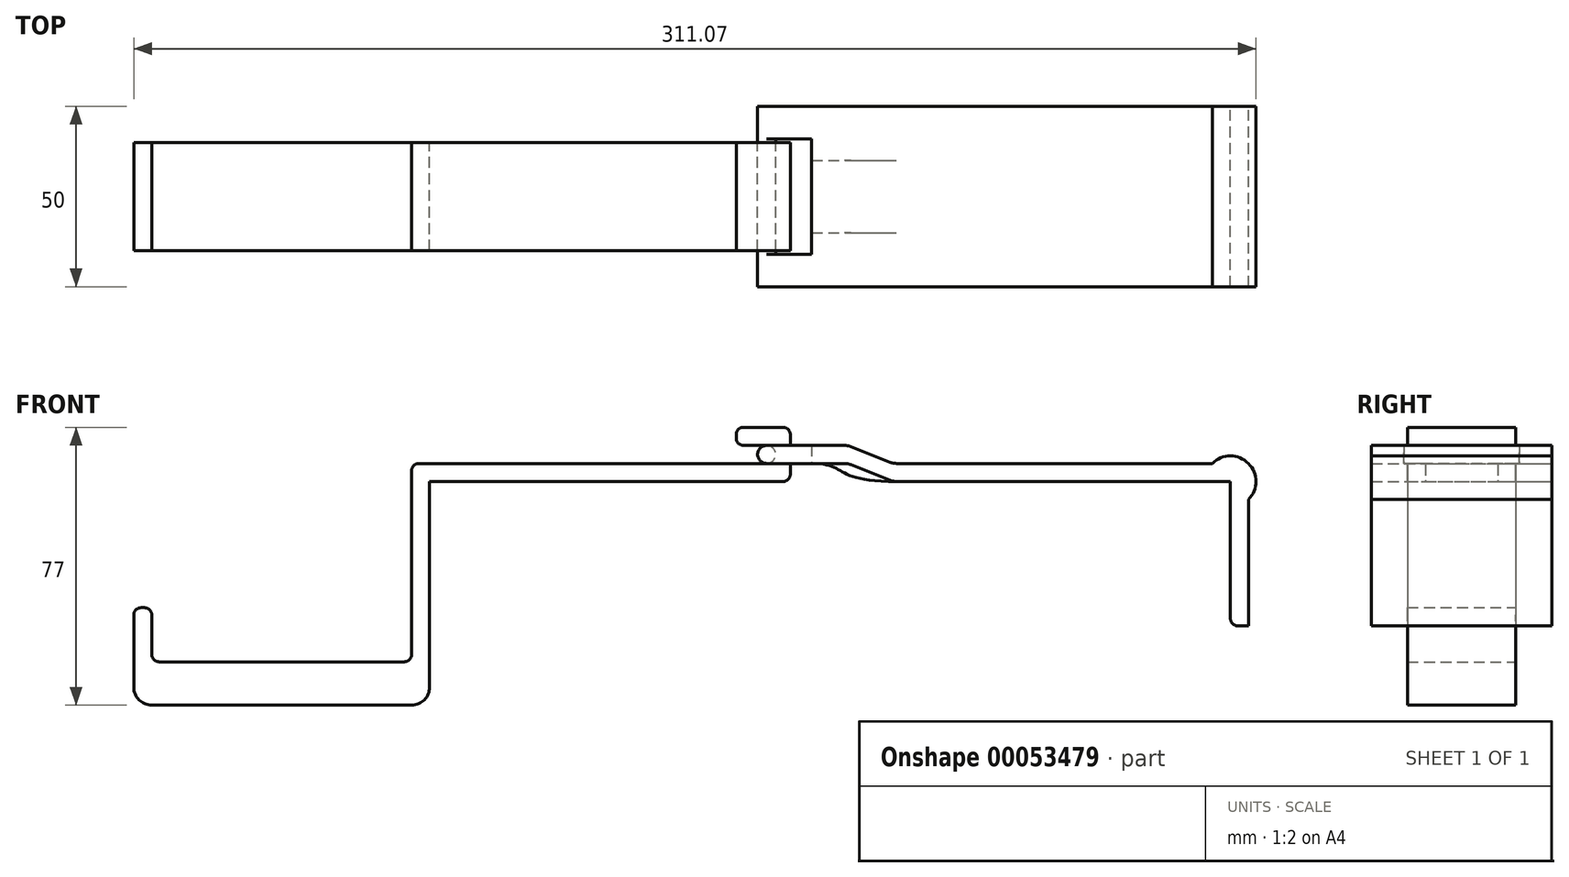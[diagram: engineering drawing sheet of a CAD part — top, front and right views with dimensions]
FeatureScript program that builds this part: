
annotation { "Feature Type Name" : "Feature", "Feature Type Description" : "" }
export const myFeature = defineFeature(function(context is Context, id is Id, definition is map)
    precondition{}
    {
        {
            var Q0;
            Q0=qCreatedBy(makeId("Front.planeOp"),FACE);
            var sketch = newSketch(context, id + "F0", { "sketchPlane" : qUnion([Q0])});
            skLineSegment(sketch, "E0.bottom", {"start": v(-111.56, 0) * mm, "end": v(110.44, 0) * mm, "construction": true});
            skLineSegment(sketch, "E0.top", {"start": v(-111.56, -365.18) * mm, "end": v(110.44, -365.18) * mm, "construction": true});
            skLineSegment(sketch, "E0.left", {"start": v(-111.56, 0) * mm, "end": v(-111.56, -365.18) * mm, "construction": true});
            skLineSegment(sketch, "E0.right", {"start": v(110.44, 0) * mm, "end": v(110.44, -365.18) * mm, "construction": true});
            skLineSegment(sketch, "E1.top", {"start": v(-111.56, 5) * mm, "end": v(-114.56, 5) * mm});
            skLineSegment(sketch, "E1.right", {"start": v(-116.56, 3) * mm, "end": v(-116.56, 50) * mm});
            skLineSegment(sketch, "E2.left", {"start": v(-111.56, 0) * mm, "end": v(-111.56, -50) * mm});
            skLineSegment(sketch, "E2.right", {"start": v(-116.56, 50) * mm, "end": v(-116.56, -48) * mm});
            skLineSegment(sketch, "E3.bottom", {"start": v(-118.56, -50) * mm, "end": v(-186.56, -50) * mm});
            skLineSegment(sketch, "E3.top", {"start": v(-116.56, -62) * mm, "end": v(-188.56, -62) * mm});
            skLineSegment(sketch, "E3.left", {"start": v(-111.56, -50) * mm, "end": v(-111.56, -57) * mm});
            skLineSegment(sketch, "E3.right", {"start": v(-193.56, -50) * mm, "end": v(-193.56, -57) * mm});
            skLineSegment(sketch, "E4.top", {"start": v(-191.56, -35) * mm, "end": v(-190.56, -35) * mm});
            skLineSegment(sketch, "E4.left", {"start": v(-193.56, -50) * mm, "end": v(-193.56, -37) * mm});
            skLineSegment(sketch, "E4.right", {"start": v(-188.56, -48) * mm, "end": v(-188.56, -37) * mm});
            skLineSegment(sketch, "E5.bottom", {"start": v(-111.56, 0) * mm, "end": v(-13.56, 0) * mm});
            skLineSegment(sketch, "E5.top", {"start": v(-111.56, 5) * mm, "end": v(-11.56, 5) * mm});
            skLineSegment(sketch, "E5.right", {"start": v(-11.56, 2) * mm, "end": v(-11.56, 5) * mm});
            skPoint(sketch, "E6.visualSharp", {"position": v(-116.56, 5) * mm});
            skArc(sketch, "E6.filletArc", {"start": v(-114.56, 5) * mm, "mid": v(-115.98, 4.41) * mm, "end": v(-116.56, 3) * mm});
            skPoint(sketch, "E7.visualSharp", {"position": v(-111.56, -62) * mm});
            skArc(sketch, "E7.filletArc", {"start": v(-116.56, -62) * mm, "mid": v(-113.03, -60.54) * mm, "end": v(-111.56, -57) * mm});
            skPoint(sketch, "E8.visualSharp", {"position": v(-193.56, -62) * mm});
            skArc(sketch, "E8.filletArc", {"start": v(-193.56, -57) * mm, "mid": v(-192.1, -60.54) * mm, "end": v(-188.56, -62) * mm});
            skPoint(sketch, "E9.visualSharp", {"position": v(-193.56, -35) * mm});
            skArc(sketch, "E9.filletArc", {"start": v(-191.56, -35) * mm, "mid": v(-192.98, -35.59) * mm, "end": v(-193.56, -37) * mm});
            skPoint(sketch, "E10.visualSharp", {"position": v(-188.56, -35) * mm});
            skArc(sketch, "E10.filletArc", {"start": v(-188.56, -37) * mm, "mid": v(-189.15, -35.59) * mm, "end": v(-190.56, -35) * mm});
            skPoint(sketch, "E11.visualSharp", {"position": v(-188.56, -50) * mm});
            skArc(sketch, "E11.filletArc", {"start": v(-188.56, -48) * mm, "mid": v(-187.98, -49.41) * mm, "end": v(-186.56, -50) * mm});
            skPoint(sketch, "E12.visualSharp", {"position": v(-116.56, -50) * mm});
            skArc(sketch, "E12.filletArc", {"start": v(-118.56, -50) * mm, "mid": v(-117.15, -49.41) * mm, "end": v(-116.56, -48) * mm});
            skLineSegment(sketch, "E13.bottom", {"start": v(-11.56, 5) * mm, "end": v(-15.64, 5) * mm});
            skLineSegment(sketch, "E13.top", {"start": v(-11.56, 10) * mm, "end": v(-15.64, 10) * mm});
            skLineSegment(sketch, "E13.left", {"start": v(-11.56, 5) * mm, "end": v(-11.56, 10) * mm});
            skLineSegment(sketch, "E13.right", {"start": v(-15.64, 5) * mm, "end": v(-15.64, 7.5) * mm});
            skLineSegment(sketch, "E14.bottom", {"start": v(-11.56, 10) * mm, "end": v(-24.56, 10) * mm});
            skLineSegment(sketch, "E14.top", {"start": v(-13.56, 15) * mm, "end": v(-24.56, 15) * mm});
            skLineSegment(sketch, "E14.left", {"start": v(-11.56, 10) * mm, "end": v(-11.56, 13) * mm});
            skLineSegment(sketch, "E14.right", {"start": v(-26.56, 12) * mm, "end": v(-26.56, 13) * mm});
            skLineSegment(sketch, "E15", {"start": v(-15.64, 7.5) * mm, "end": v(-18.14, 7.5) * mm, "construction": true});
            skPoint(sketch, "E15.endSnap0", {"position": v(-15.64, 7.5) * mm});
            skLineSegment(sketch, "E16", {"start": v(-15.64, 7.5) * mm, "end": v(-15.64, 10) * mm});
            skCircle(sketch, "E17", {"center": v(-18.14, 7.5) * mm, "radius": 2.5 * mm});
            skLineSegment(sketch, "E18.bottom", {"start": v(-18.14, 10) * mm, "end": v(-5.64, 10) * mm});
            skLineSegment(sketch, "E18.top", {"start": v(-18.14, 5) * mm, "end": v(3.4, 5) * mm});
            skLineSegment(sketch, "E18.left", {"start": v(-18.14, 10) * mm, "end": v(-18.14, 5) * mm});
            skLineSegment(sketch, "E19", {"start": v(-5.64, 10) * mm, "end": v(3.4, 10) * mm});
            skPoint(sketch, "E20.visualSharp", {"position": v(-26.56, 15) * mm});
            skArc(sketch, "E20.filletArc", {"start": v(-24.56, 15) * mm, "mid": v(-25.98, 14.41) * mm, "end": v(-26.56, 13) * mm});
            skPoint(sketch, "E21.visualSharp", {"position": v(-26.56, 10) * mm});
            skArc(sketch, "E21.filletArc", {"start": v(-26.56, 12) * mm, "mid": v(-25.98, 10.59) * mm, "end": v(-24.56, 10) * mm});
            skPoint(sketch, "E22.visualSharp", {"position": v(-11.56, 15) * mm});
            skArc(sketch, "E22.filletArc", {"start": v(-11.56, 13) * mm, "mid": v(-12.15, 14.41) * mm, "end": v(-13.56, 15) * mm});
            skPoint(sketch, "E23.visualSharp", {"position": v(-11.56, 0) * mm});
            skArc(sketch, "E23.filletArc", {"start": v(-13.56, 0) * mm, "mid": v(-12.15, 0.59) * mm, "end": v(-11.56, 2) * mm});
            skLineSegment(sketch, "E24", {"start": v(-5.64, 10) * mm, "end": v(-5.64, 5) * mm});
            skLineSegment(sketch, "E25", {"start": v(4.36, 10) * mm, "end": v(4.36, 5) * mm});
            skLineSegment(sketch, "E26", {"start": v(5.26, 9.64) * mm, "end": v(15.97, 5.36) * mm});
            skLineSegment(sketch, "E27.bottom", {"start": v(17.83, 5) * mm, "end": v(105.44, 5) * mm});
            skLineSegment(sketch, "E27.top", {"start": v(17.83, 0) * mm, "end": v(110.44, 0) * mm});
            skLineSegment(sketch, "E28", {"start": v(16.86, 5) * mm, "end": v(16.86, 0) * mm, "construction": true});
            skLineSegment(sketch, "E29", {"start": v(5.26, 4.64) * mm, "end": v(15.97, 0.36) * mm});
            skLineSegment(sketch, "E30.top", {"start": v(112.44, -40) * mm, "end": v(115.44, -40) * mm});
            skLineSegment(sketch, "E30.left", {"start": v(110.44, 0) * mm, "end": v(110.44, -38) * mm});
            skLineSegment(sketch, "E30.right", {"start": v(115.44, -5) * mm, "end": v(115.44, -40) * mm});
            skArc(sketch, "E31", {"start": v(115.44, -5) * mm, "mid": v(115.44, 5) * mm, "end": v(105.44, 5) * mm});
            skPoint(sketch, "E32.top.end.orphan", {"position": v(115.44, 0) * mm});
            skPoint(sketch, "E33.visualSharp", {"position": v(110.44, -40) * mm});
            skArc(sketch, "E33.filletArc", {"start": v(110.44, -38) * mm, "mid": v(111.02, -39.41) * mm, "end": v(112.44, -40) * mm});
            skPoint(sketch, "E34.visualSharp", {"position": v(16.86, 5) * mm});
            skArc(sketch, "E34.filletArc", {"start": v(15.97, 5.36) * mm, "mid": v(16.88, 5.1) * mm, "end": v(17.83, 5) * mm});
            skPoint(sketch, "E35.visualSharp", {"position": v(4.36, 5) * mm});
            skArc(sketch, "E35.filletArc", {"start": v(5.26, 4.64) * mm, "mid": v(4.35, 4.9) * mm, "end": v(3.4, 5) * mm});
            skPoint(sketch, "E36.visualSharp", {"position": v(4.36, 10) * mm});
            skArc(sketch, "E36.filletArc", {"start": v(5.26, 9.64) * mm, "mid": v(4.35, 9.9) * mm, "end": v(3.4, 10) * mm});
            skPoint(sketch, "E37.visualSharp", {"position": v(16.86, 0) * mm});
            skArc(sketch, "E37.filletArc", {"start": v(15.97, 0.36) * mm, "mid": v(16.88, 0.1) * mm, "end": v(17.83, 0) * mm});
            skFitSpline(sketch, "E38", {"points": [v(-5.64, 5) * mm, v(17.83, 0) * mm], "startDerivative": vector(30, 0) * mm, "endDerivative": vector(53.48, 0) * mm});
            skSolve(sketch);
        }
        {
            var Q0;
            Q0=makeQuery(id+"F0.imprint","IMPRINT",FACE,{"disambiguationData":[TD([[makeQuery(id+"F0.imprint","IMPRINT",EDGE,{"derivedFrom":sQuery(id+"F0.wireOp",EDGE,"E1.top")}),1.0]])]});
            var Q1;
            {var subQ2=sQuery(id+"F0.wireOp",EDGE,"E14.bottom");Q1=makeQuery(id+"F0.imprint","IMPRINT",FACE,{"disambiguationData":[TD([[makeQuery(id+"F0.imprint","IMPRINT",EDGE,{"derivedFrom":subQ2}),-1.0]])]});}
            var Q2;
            {var subQ0=sQuery(id+"F0.wireOp",EDGE,"E16");Q2=makeQuery(id+"F0.imprint","IMPRINT",FACE,{"disambiguationData":[TD([[makeQuery(id+"F0.imprint","IMPRINT",EDGE,{"derivedFrom":subQ0}),1.0]])]});}
            var Q3;
            {var subQ1=sQuery(id+"F0.wireOp",EDGE,"E13.left");Q3=makeQuery(id+"F0.imprint","IMPRINT",FACE,{"disambiguationData":[TD([[makeQuery(id+"F0.imprint","IMPRINT",EDGE,{"derivedFrom":subQ1}),1.0]])]});}
            var Q4;
            {var subQ0=sQuery(id+"F0.wireOp",EDGE,"E13.right");Q4=makeQuery(id+"F0.imprint","IMPRINT",FACE,{"disambiguationData":[TD([[makeQuery(id+"F0.imprint","IMPRINT",EDGE,{"derivedFrom":subQ0}),1.0]])]});}
            extrude(context, id + "F1", {"entities" : qUnion([Q0, Q1, Q2, Q3, Q4]), "depth" : 15 * mm, "hasSecondDirection" : true, "secondDirectionOppositeDirection" : true, "secondDirectionDepth" : 15 * mm});
        }
        {
            var Q0;
            {var subQ0=sQuery(id+"F0.wireOp",EDGE,"E18.left");Q0=makeQuery(id+"F0.imprint","IMPRINT",FACE,{"disambiguationData":[TD([[makeQuery(id+"F0.imprint","IMPRINT",EDGE,{"derivedFrom":subQ0}),-1.0]])]});}
            var Q1;
            {var subQ2=sQuery(id+"F0.wireOp",EDGE,"E18.left");Q1=makeQuery(id+"F0.imprint","IMPRINT",FACE,{"disambiguationData":[TD([[makeQuery(id+"F0.imprint","IMPRINT",EDGE,{"derivedFrom":subQ2}),1.0]])]});}
            var Q2;
            {var subQ0=sQuery(id+"F0.wireOp",EDGE,"E16");Q2=makeQuery(id+"F0.imprint","IMPRINT",FACE,{"disambiguationData":[TD([[makeQuery(id+"F0.imprint","IMPRINT",EDGE,{"derivedFrom":subQ0}),1.0]])]});}
            var Q3;
            {var subQ0=sQuery(id+"F0.wireOp",EDGE,"E13.right");Q3=makeQuery(id+"F0.imprint","IMPRINT",FACE,{"disambiguationData":[TD([[makeQuery(id+"F0.imprint","IMPRINT",EDGE,{"derivedFrom":subQ0}),1.0]])]});}
            var Q4;
            {var subQ1=sQuery(id+"F0.wireOp",EDGE,"E13.left");Q4=makeQuery(id+"F0.imprint","IMPRINT",FACE,{"disambiguationData":[TD([[makeQuery(id+"F0.imprint","IMPRINT",EDGE,{"derivedFrom":subQ1}),1.0]])]});}
            var Q5;
            {var subQ0=sQuery(id+"F0.wireOp",EDGE,"E13.left");Q5=makeQuery(id+"F0.imprint","IMPRINT",FACE,{"disambiguationData":[TD([[makeQuery(id+"F0.imprint","IMPRINT",EDGE,{"derivedFrom":subQ0}),-1.0]])]});}
            var Q6;
            {var subQ1=sQuery(id+"F0.wireOp",EDGE,"E19");Q6=makeQuery(id+"F0.imprint","IMPRINT",FACE,{"disambiguationData":[TD([[makeQuery(id+"F0.imprint","IMPRINT",EDGE,{"derivedFrom":subQ1}),-1.0]])]});}
            extrude(context, id + "F2", {"entities" : qUnion([Q0, Q1, Q2, Q3, Q4, Q5, Q6]), "depth" : 25 * mm, "hasSecondDirection" : true, "secondDirectionOppositeDirection" : true, "secondDirectionDepth" : 25 * mm});
        }
        {
            var Q0;
            {var subQ0=sQuery(id+"F0.wireOp",EDGE,"E16");Q0=makeQuery(id+"F0.imprint","IMPRINT",FACE,{"disambiguationData":[TD([[makeQuery(id+"F0.imprint","IMPRINT",EDGE,{"derivedFrom":subQ0}),1.0]])]});}
            var Q1;
            {var subQ0=sQuery(id+"F0.wireOp",EDGE,"E13.right");Q1=makeQuery(id+"F0.imprint","IMPRINT",FACE,{"disambiguationData":[TD([[makeQuery(id+"F0.imprint","IMPRINT",EDGE,{"derivedFrom":subQ0}),1.0]])]});}
            var Q2;
            {var subQ1=sQuery(id+"F0.wireOp",EDGE,"E13.left");Q2=makeQuery(id+"F0.imprint","IMPRINT",FACE,{"disambiguationData":[TD([[makeQuery(id+"F0.imprint","IMPRINT",EDGE,{"derivedFrom":subQ1}),1.0]])]});}
            var Q3;
            {var subQ0=sQuery(id+"F0.wireOp",EDGE,"E13.left");Q3=makeQuery(id+"F0.imprint","IMPRINT",FACE,{"disambiguationData":[TD([[makeQuery(id+"F0.imprint","IMPRINT",EDGE,{"derivedFrom":subQ0}),-1.0]])]});}
            extrude(context, id + "F3", {"entities" : qUnion([Q0, Q1, Q2, Q3]), "operationType" : NewBodyOperationType.REMOVE, "oppositeDirection" : true, "depth" : 16 * mm, "hasSecondDirection" : true, "secondDirectionOppositeDirection" : false, "secondDirectionDepth" : 16 * mm});
        }
        {
            var Q0;
            Q0=makeQuery(id+"F0.imprint","IMPRINT",FACE,{"disambiguationData":[TD([[makeQuery(id+"F0.imprint","IMPRINT",EDGE,{"derivedFrom":sQuery(id+"F0.wireOp",EDGE,"E29")}),-1.0]])]});
            extrude(context, id + "F4", {"entities" : qUnion([Q0]), "operationType" : NewBodyOperationType.ADD, "depth" : 10 * mm, "hasSecondDirection" : true, "secondDirectionOppositeDirection" : true, "secondDirectionDepth" : 10 * mm});
        }
    });
